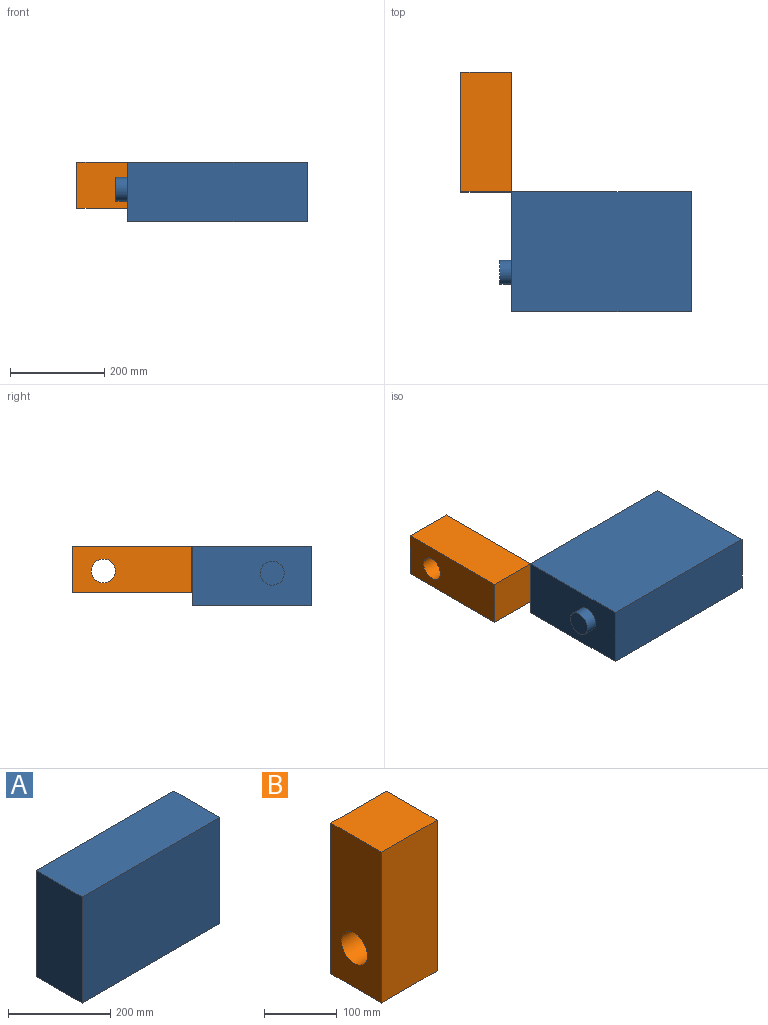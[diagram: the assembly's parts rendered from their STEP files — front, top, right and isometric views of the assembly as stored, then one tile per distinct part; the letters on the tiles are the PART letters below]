
ASSEMBLY  parts=2 mates=1
PART A: 8 faces, bbox 406.4x127x254 mm
  f0: plane 254x127mm, normal (-1,0,0), area 32258mm2, adj f1,f3,f4,f5
  f1: plane 381x127mm, normal (0,0,-1), area 48387mm2, adj f0,f2,f4,f5
  f2: plane 254x127mm, normal (1,0,0), area 30231.2mm2, adj f1,f3,f4,f5,f6
  f3: plane 381x127mm, normal (0,0,1), area 48387mm2, adj f0,f2,f4,f5
  f4: plane 381x254mm, normal (0,-1,0), area 96774mm2, adj f0,f1,f2,f3
  f5: plane 381x254mm, normal (0,1,0), area 96774mm2, adj f0,f1,f2,f3
  f6: cylinder r=25.4mm len=50.8mm, axis (-1,0,0), area 4053.7mm2, adj f2,f7
  f7: plane 50.8x50.8mm, normal (1,0,0), area 2026.8mm2, adj f6
PART B: 7 faces, bbox 108.2x98.5x254 mm
  f0: plane 254x108.17mm, normal (0,1,0), area 27474.7mm2, adj f1,f3,f4,f5
  f1: plane 254x98.5mm, normal (-1,0,0), area 22993mm2, adj f0,f2,f4,f5,f6
  f2: plane 254x108.17mm, normal (0,-1,0), area 27474.7mm2, adj f1,f3,f4,f5
  f3: plane 254x98.5mm, normal (1,0,0), area 22993mm2, adj f0,f2,f4,f5,f6
  f4: plane 108.17x98.5mm, normal (0,0,1), area 10654.9mm2, adj f0,f1,f2,f3
  f5: plane 108.17x98.5mm, normal (0,0,-1), area 10654.9mm2, adj f0,f1,f2,f3
  f6: cylinder r=25.4mm len=108.17mm, axis (1,0,0), area 17262.9mm2, adj f1,f3
PLACE A rot(axis=(0,-0.71,-0.71),180deg) t=(924.05,141.39,-166.85)mm
PLACE B rot(axis=(0,0.71,-0.71),180deg) t=(543.05,649.39,-265.35)mm
MATE planar B.f4 <-> A.f3  axis (0,-1,0) through (543.05,395.39,-166.85)mm
